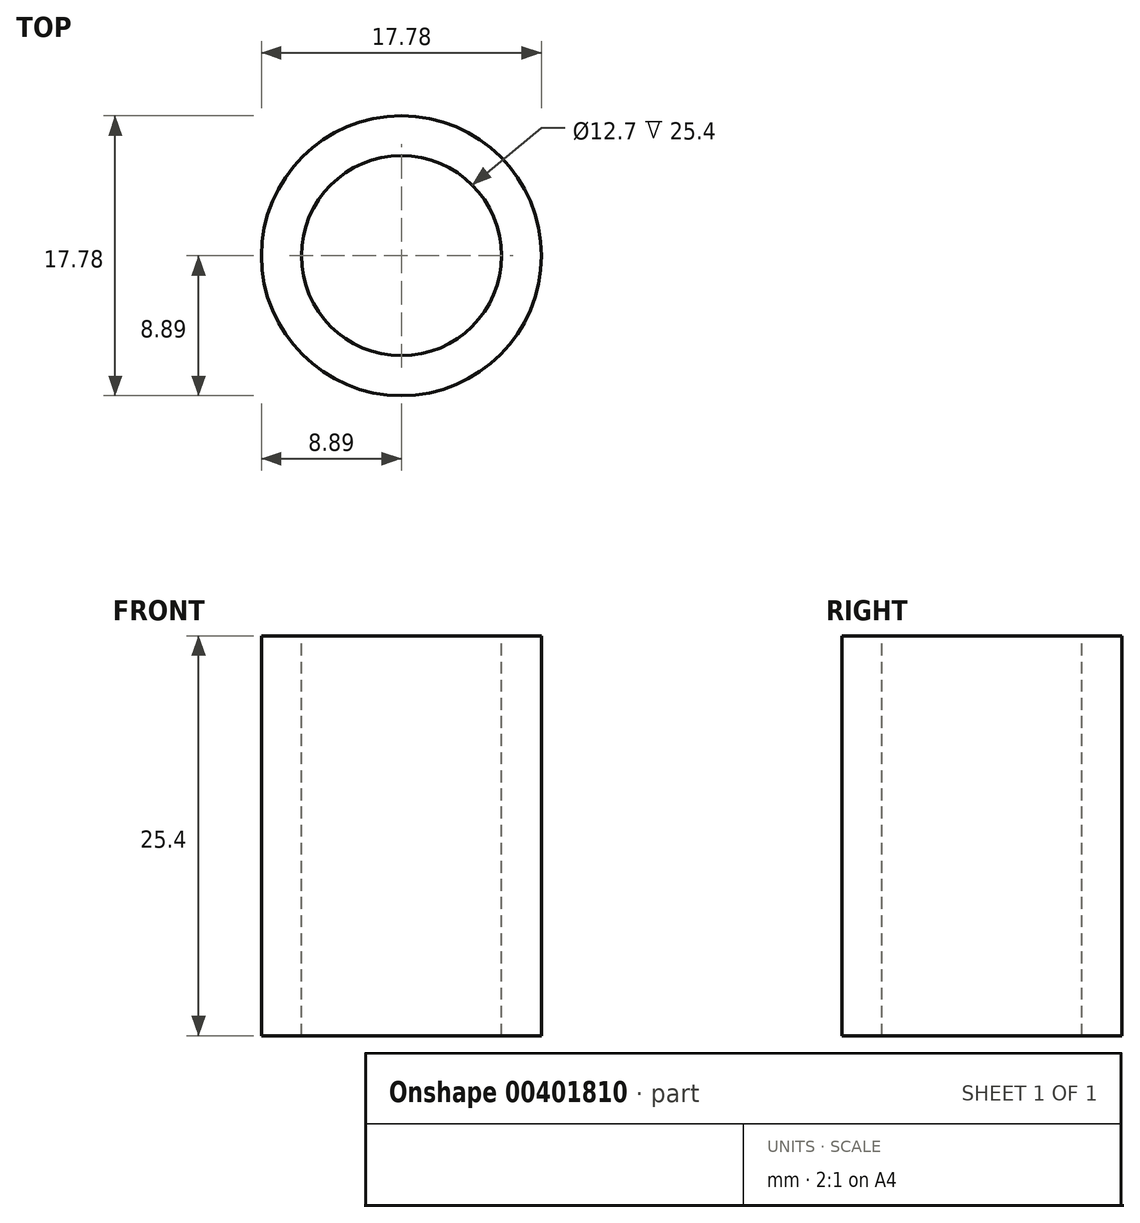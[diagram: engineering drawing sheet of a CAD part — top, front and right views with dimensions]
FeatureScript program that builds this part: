
annotation { "Feature Type Name" : "Feature", "Feature Type Description" : "" }
export const myFeature = defineFeature(function(context is Context, id is Id, definition is map)
    precondition{}
    {
        {
            var Q0;
            Q0=qCreatedBy(makeId("Top.planeOp"),FACE);
            var sketch = newSketch(context, id + "F0", { "sketchPlane" : qUnion([Q0])});
            skCircle(sketch, "E0", {"center": v(0, 0) * mm, "radius": 8.9 * mm});
            skSolve(sketch);
        }
        {
            var Q0;
            Q0 = qSketchRegion(id + "F0", true);
            extrude(context, id + "F1", {"entities" : qUnion([Q0]), "depth" : 25.4 * mm});
        }
        {
            var Q0;
            Q0=makeQuery(id+"F1.opExtrude","CAP_FACE",FACE,{"disambiguationData":[OSD([sQuery(id+"F0.wireOp",EDGE,"E0")])],"isStart":false});
            var sketch = newSketch(context, id + "F2", { "sketchPlane" : qUnion([Q0])});
            skCircle(sketch, "E1", {"center": v(0, 0) * mm, "radius": 6.35 * mm});
            skSolve(sketch);
        }
        {
            var Q0;
            Q0 = qSketchRegion(id + "F2", true);
            extrude(context, id + "F3", {"entities" : qUnion([Q0]), "operationType" : NewBodyOperationType.REMOVE, "oppositeDirection" : true, "depth" : 34.87 * mm});
        }
        {
            var Q0;
            Q0=qCreatedBy(makeId("Top.planeOp"),FACE);
            cPlane(context, id + "F4", {"entities" : qUnion([Q0]), "cplaneType" : CPlaneType.OFFSET, "offset" : 7.62 * mm, "width" : 152.4 * mm, "height" : 152.4 * mm});
        }
        {
            var Q0;
            Q0=qCreatedBy(id+"F4.planeOp",FACE);
            var sketch = newSketch(context, id + "F5", { "sketchPlane" : qUnion([Q0])});
            skCircle(sketch, "E2", {"center": v(0, 0) * mm, "radius": 8.9 * mm});
            skSolve(sketch);
        }
        {
            var Q0;
            Q0 = qConstructionFilter(qBodyType(qCreatedBy(id + "F5" ,EDGE), BodyType.WIRE), ConstructionObject.NO);
            extrude(context, id + "F6", {"bodyType" : ToolBodyType.SURFACE, "operationType" : NewBodyOperationType.REMOVE, "surfaceEntities" : qUnion([Q0]), "depth" : 5.08 * mm});
        }
    });
